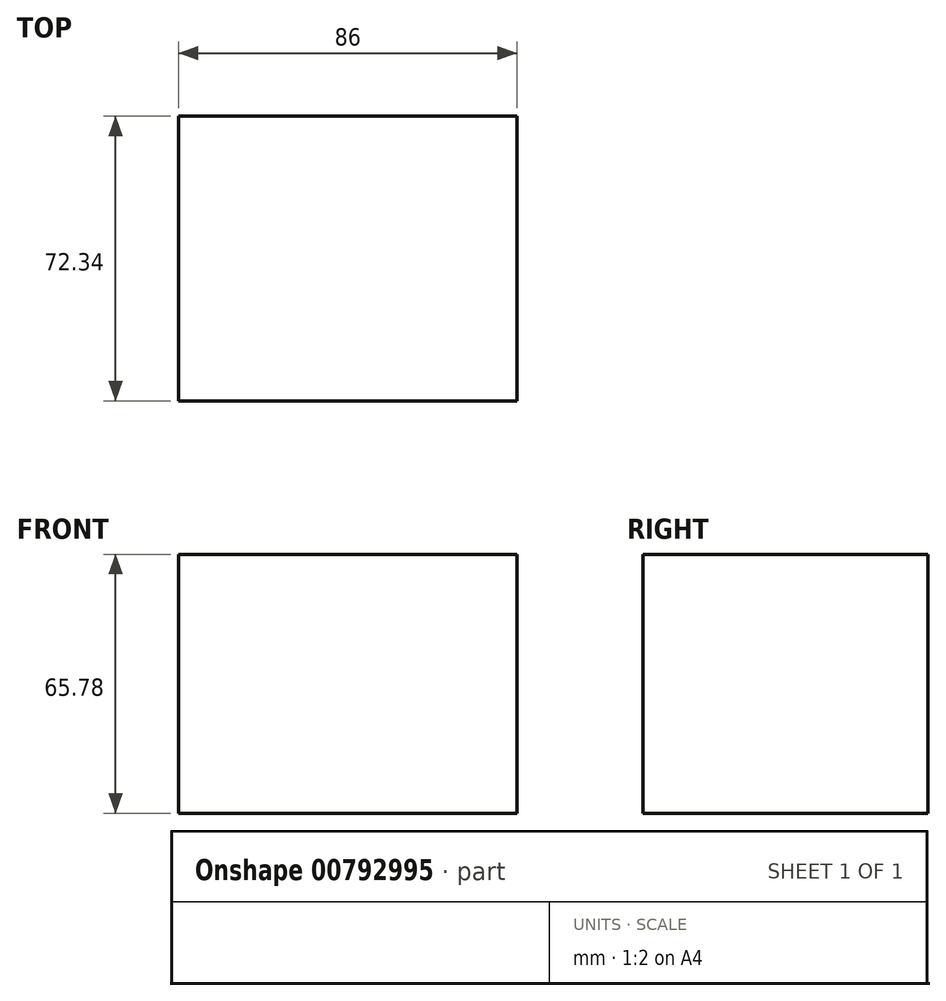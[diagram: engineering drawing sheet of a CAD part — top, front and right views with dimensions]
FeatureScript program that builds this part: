
annotation { "Feature Type Name" : "Feature", "Feature Type Description" : "" }
export const myFeature = defineFeature(function(context is Context, id is Id, definition is map)
    precondition{}
    {
        {
            var Q0;
            Q0=qCreatedBy(makeId("Right.planeOp"),FACE);
            var sketch = newSketch(context, id + "F0", { "sketchPlane" : qUnion([Q0])});
            skLineSegment(sketch, "E0.bottom", {"start": v(-19.3, -15.37) * mm, "end": v(53.05, -15.37) * mm});
            skLineSegment(sketch, "E0.top", {"start": v(-19.3, 50.41) * mm, "end": v(53.05, 50.41) * mm});
            skLineSegment(sketch, "E0.left", {"start": v(-19.3, -15.37) * mm, "end": v(-19.3, 50.41) * mm});
            skLineSegment(sketch, "E0.right", {"start": v(53.05, -15.37) * mm, "end": v(53.05, 50.41) * mm});
            skSolve(sketch);
        }
        {
            var Q0;
            Q0=makeQuery(id+"F0.imprint","IMPRINT",FACE,{"disambiguationData":[TD([[makeQuery(id+"F0.imprint","IMPRINT",EDGE,{"derivedFrom":sQuery(id+"F0.wireOp",EDGE,"E0.bottom")}),1.0]])]});
            extrude(context, id + "F1", {"entities" : qUnion([Q0]), "depth" : 61 * mm, "offsetDistance" : 25 * mm});
        }
        {
            var Q0;
            Q0=makeQuery(id+"F1.opExtrude","CAP_FACE",FACE,{"disambiguationData":[OSD([sQuery(id+"F0.wireOp",EDGE,"E0.bottom"),sQuery(id+"F0.wireOp",EDGE,"E0.top"),sQuery(id+"F0.wireOp",EDGE,"E0.left"),sQuery(id+"F0.wireOp",EDGE,"E0.right")])],"isStart":false});
            var Q1;
            Q1=makeQuery(id+"F1.opExtrude","CAP_FACE",FACE,{"disambiguationData":[OSD([sQuery(id+"F0.wireOp",EDGE,"E0.bottom"),sQuery(id+"F0.wireOp",EDGE,"E0.top"),sQuery(id+"F0.wireOp",EDGE,"E0.left"),sQuery(id+"F0.wireOp",EDGE,"E0.right")])],"isStart":true});
            extrude(context, id + "F2", {"entities" : qUnion([Q0, Q1]), "operationType" : NewBodyOperationType.ADD, "depth" : 25 * mm, "offsetDistance" : 25 * mm});
        }
    });
